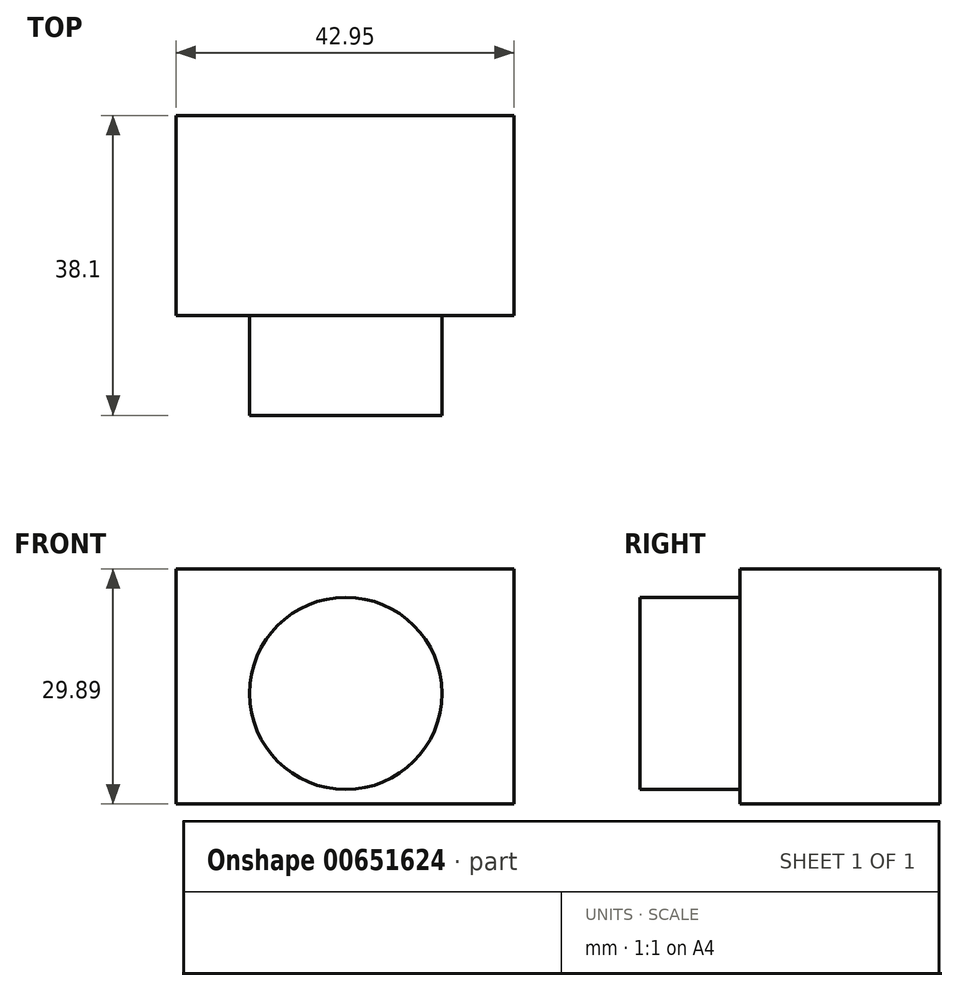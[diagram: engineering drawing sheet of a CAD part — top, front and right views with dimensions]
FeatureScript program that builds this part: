
annotation { "Feature Type Name" : "Feature", "Feature Type Description" : "" }
export const myFeature = defineFeature(function(context is Context, id is Id, definition is map)
    precondition{}
    {
        {
            var Q0;
            Q0=qCreatedBy(makeId("Front.planeOp"),FACE);
            var sketch = newSketch(context, id + "F0", { "sketchPlane" : qUnion([Q0])});
            skLineSegment(sketch, "E0.bottom", {"start": v(-15.57, -6.8) * mm, "end": v(-58.52, -6.8) * mm});
            skLineSegment(sketch, "E0.top", {"start": v(-15.57, 23.1) * mm, "end": v(-58.52, 23.1) * mm});
            skLineSegment(sketch, "E0.left", {"start": v(-15.57, -6.8) * mm, "end": v(-15.57, 23.1) * mm});
            skLineSegment(sketch, "E0.right", {"start": v(-58.52, -6.8) * mm, "end": v(-58.52, 23.1) * mm});
            skSolve(sketch);
        }
        {
            var Q0;
            Q0 = qSketchRegion(id + "F0", true);
            extrude(context, id + "F1", {"entities" : qUnion([Q0]), "depth" : 25.4 * mm, "offsetDistance" : 25.4 * mm});
        }
        {
            var Q0;
            Q0=makeQuery(id+"F1.opExtrude","CAP_FACE",FACE,{"disambiguationData":[OSD([sQuery(id+"F0.wireOp",EDGE,"E0.bottom"),sQuery(id+"F0.wireOp",EDGE,"E0.top"),sQuery(id+"F0.wireOp",EDGE,"E0.left"),sQuery(id+"F0.wireOp",EDGE,"E0.right")])],"isStart":false});
            var sketch = newSketch(context, id + "F2", { "sketchPlane" : qUnion([Q0])});
            skCircle(sketch, "E1", {"center": v(-36.97, 7.27) * mm, "radius": 12.21 * mm});
            skSolve(sketch);
        }
        {
            var Q0;
            Q0=makeQuery(id+"F2.imprint","IMPRINT",FACE,{"disambiguationData":[TD([[makeQuery(id+"F2.imprint","IMPRINT",EDGE,{"derivedFrom":sQuery(id+"F2.wireOp",EDGE,"E1")}),1.0]])]});
            extrude(context, id + "F3", {"entities" : qUnion([Q0]), "operationType" : NewBodyOperationType.ADD, "depth" : 12.7 * mm, "offsetDistance" : 25.4 * mm});
        }
    });
